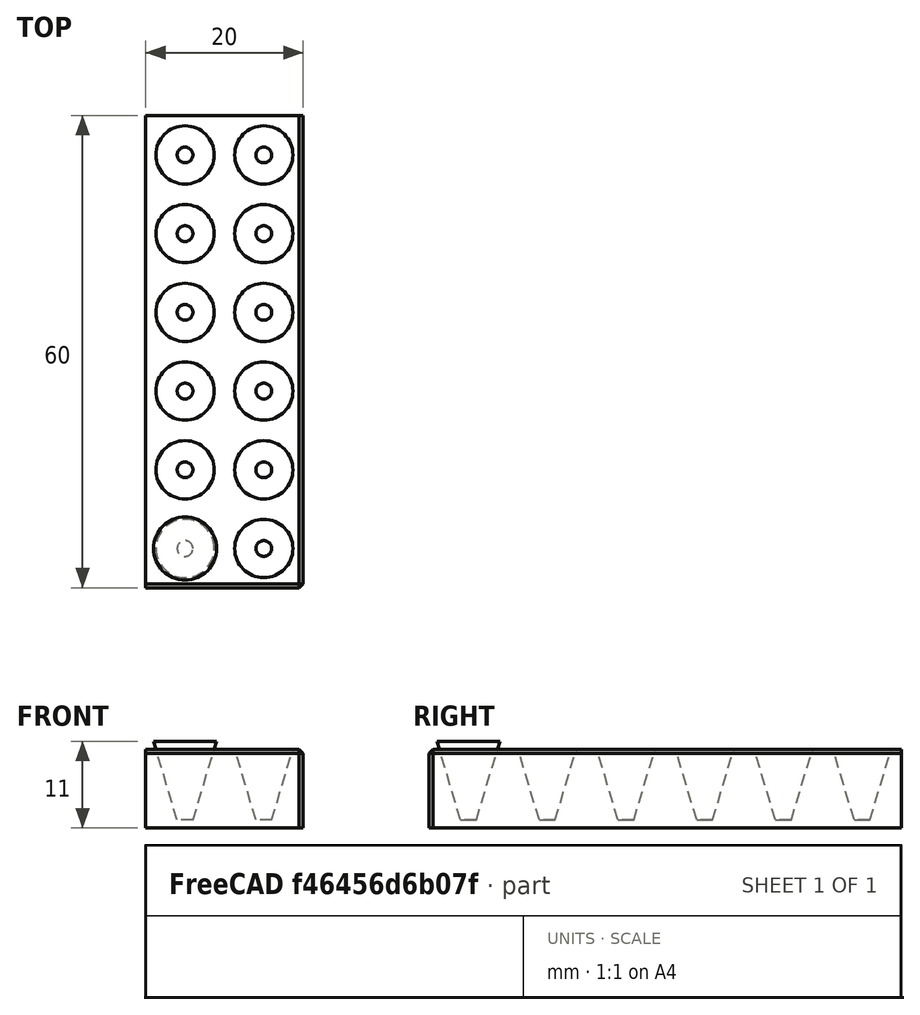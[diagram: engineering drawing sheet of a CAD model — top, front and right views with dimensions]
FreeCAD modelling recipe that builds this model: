
FCSTD DOCUMENT  (FreeCAD 0.21R33694 (Git))
Label: cartacho_repte2
License: All rights reserved
LicenseURL: http://en.wikipedia.org/wiki/All_rights_reserved
objects: Part::Box×1, Part::Cone×1, Part::FeaturePython×1, Part::Cut×1, Part::Chamfer×1
note: 4 computed .brp shape members not serialized (recipe doc carries the construction recipe); baked Part::Feature solids carry a one-line shape summary decoded from their .brp

FEATURE [Part::Box] Box  label="Cube"
  AttacherType = Attacher::AttachEngine3D
  Height = 10
  Length = 20
  Width = 60
FEATURE [Part::Cone] Cone
  Angle = 360
  AttacherType = Attacher::AttachEngine3D
  Height = 10
  Placement = pos=(5,5,1) rot=(0,0,1;0rad)
  Radius1 = 1
  Radius2 = 4
FEATURE [Part::FeaturePython] Array  # Draft array (typed FeaturePython)
  AlwaysSyncPlacement = false
  Angle = 360
  ArrayType = 0
  Axis = (0,0,1)
  Base = -> Cone
  Center = (0,0,0)
  Count = 12
  ExpandArray = false
  Fuse = false
  IntervalAxis = (0,0,0)
  IntervalX = (10,0,0)
  IntervalY = (0,10,0)
  IntervalZ = (0,0,100)
  NumberCircles = 3
  NumberPolar = 5
  NumberX = 2
  NumberY = 6
  NumberZ = 1
  PlacementList = 12 placements: [(5,5,1),(5,15,1),(5,25,1),(5,35,1),(5,45,1),(5,55,1),(15,5,1),(15,15,1),(15,25,1),(15,35,1),(15,45,1),(15,55,1)]
  RadialDistance = 50
  ScaleList = (12) [(1,1,1),(1,1,1),(1,1,1),(1,1,1),(1,1,1),(1,1,1),(1,1,1),(1,1,1),(1,1,1),(1,1,1),(1,1,1),(1,1,1)]
  Symmetry = 1
  TangentialDistance = 25
FEATURE [Part::Cut] Cut
  Base = -> Box
  Refine = true
  Tool = -> Array
FEATURE [Part::Chamfer] Chamfer
  Base = -> Cut
  Edges = 3 edges r=0.5: [Edge6,Edge7,Edge9]
